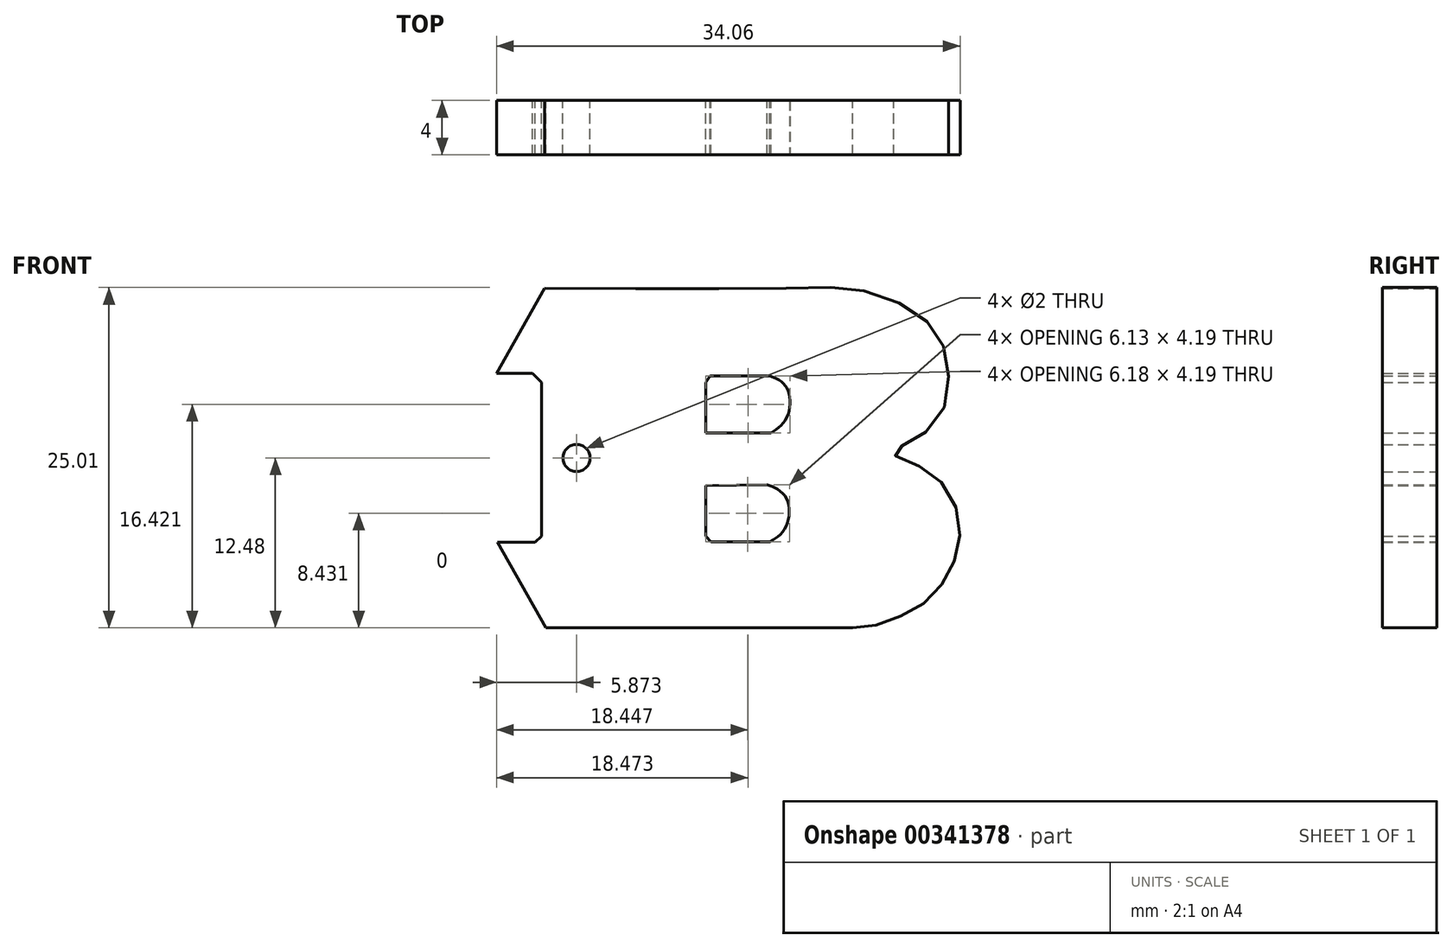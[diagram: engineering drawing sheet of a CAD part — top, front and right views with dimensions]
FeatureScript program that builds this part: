
annotation { "Feature Type Name" : "Feature", "Feature Type Description" : "" }
export const myFeature = defineFeature(function(context is Context, id is Id, definition is map)
    precondition{}
    {
        {
            var Q0;
            Q0=qCreatedBy(makeId("Front.planeOp"),FACE);
            var sketch = newSketch(context, id + "F0", { "sketchPlane" : qUnion([Q0])});
            skLineSegment(sketch, "E0", {"start": v(-1.02, 5.57) * mm, "end": v(-1.02, 1.85) * mm});
            skLineSegment(sketch, "E1", {"start": v(-1.02, 1.85) * mm, "end": v(3.76, 1.85) * mm});
            skLineSegment(sketch, "E2", {"start": v(3.68, 6.03) * mm, "end": v(-0.71, 6.03) * mm});
            skLineSegment(sketch, "E3", {"start": v(-0.71, 6.03) * mm, "end": v(-1.02, 5.57) * mm});
            skLineSegment(sketch, "E4", {"start": v(-1.02, -2.02) * mm, "end": v(-1.02, -5.76) * mm});
            skLineSegment(sketch, "E5", {"start": v(-1.02, -5.76) * mm, "end": v(-0.64, -6.14) * mm});
            skLineSegment(sketch, "E6", {"start": v(-0.64, -6.14) * mm, "end": v(3.68, -6.14) * mm});
            skLineSegment(sketch, "E7", {"start": v(-1.02, -2.02) * mm, "end": v(3.47, -1.95) * mm});
            skFitSpline(sketch, "E8", {"points": [v(3.68, -6.14) * mm, v(4.53, -5.54) * mm, v(5.05, -4.42) * mm, v(4.98, -3.13) * mm, v(4.25, -2.3) * mm, v(3.47, -1.95) * mm], "startDerivative": vector(4.7, 2.6) * mm, "endDerivative": vector(-4.47, 1.6) * mm});
            skFitSpline(sketch, "E9", {"points": [v(3.76, 1.85) * mm, v(4.58, 2.48) * mm, v(5.11, 3.54) * mm, v(5.07, 4.76) * mm, v(4.62, 5.53) * mm, v(3.68, 6.03) * mm], "startDerivative": vector(4.46, 2.83) * mm, "endDerivative": vector(-5.25, 2.14) * mm});
            skLineSegment(sketch, "E10", {"start": v(-12.8, -12.48) * mm, "end": v(9.75, -12.48) * mm});
            skFitSpline(sketch, "E11", {"points": [v(9.75, -12.48) * mm, v(11.48, -12.3) * mm, v(13.49, -11.51) * mm, v(15.31, -10.43) * mm, v(16.66, -8.76) * mm, v(17.48, -6.76) * mm, v(17.57, -4.42) * mm, v(16.44, -1.98) * mm, v(14.64, -0.58) * mm, v(12.84, 0.23) * mm, v(12.84, 0.57) * mm, v(14.1, 1.23) * mm, v(16.2, 3.12) * mm, v(16.82, 6.01) * mm, v(16.16, 8.8) * mm, v(14.12, 10.9) * mm, v(10.27, 12.35) * mm, v(6.04, 12.5) * mm, v(-12.87, 12.49) * mm], "startDerivative": vector(39.24, 1.65) * mm, "endDerivative": vector(-156.24, 0.65) * mm});
            skFitSpline(sketch, "E12", {"points": [v(-12.87, 12.49) * mm, v(-16.4, 6.2) * mm], "startDerivative": vector(-3.52, -6.28) * mm, "endDerivative": vector(-3.52, -6.28) * mm});
            skFitSpline(sketch, "E13", {"points": [v(-16.4, 6.2) * mm, v(-13.78, 6.2) * mm], "startDerivative": vector(2.62, 0) * mm, "endDerivative": vector(2.62, 0) * mm});
            skFitSpline(sketch, "E14", {"points": [v(-13.78, 6.2) * mm, v(-13.08, 5.55) * mm], "startDerivative": vector(0.7, -0.66) * mm, "endDerivative": vector(0.7, -0.66) * mm});
            skFitSpline(sketch, "E15", {"points": [v(-13.08, 5.55) * mm, v(-13.08, -5.75) * mm], "startDerivative": vector(0, -11.3) * mm, "endDerivative": vector(0, -11.3) * mm});
            skFitSpline(sketch, "E16", {"points": [v(-13.08, -5.75) * mm, v(-13.58, -6.2) * mm], "startDerivative": vector(-0.5, -0.45) * mm, "endDerivative": vector(-0.5, -0.45) * mm});
            skFitSpline(sketch, "E17", {"points": [v(-13.58, -6.2) * mm, v(-16.33, -6.2) * mm], "startDerivative": vector(-2.75, 0) * mm, "endDerivative": vector(-2.75, 0) * mm});
            skFitSpline(sketch, "E18", {"points": [v(-16.33, -6.2) * mm, v(-12.8, -12.48) * mm], "startDerivative": vector(3.54, -6.29) * mm, "endDerivative": vector(3.54, -6.29) * mm});
            skFitSpline(sketch, "E19", {"points": [v(-14.26, 13.78) * mm, v(10.52, 13.65) * mm], "startDerivative": vector(24.77, -0.13) * mm, "endDerivative": vector(24.77, -0.13) * mm});
            skFitSpline(sketch, "E20", {"points": [v(10.52, 13.65) * mm, v(14.21, 12.74) * mm, v(17.38, 10.62) * mm, v(18.6, 7.28) * mm, v(18.3, 3.41) * mm, v(15.72, 0.7) * mm], "startDerivative": vector(18.49, -3.32) * mm, "endDerivative": vector(-15.59, -12.12) * mm});
            skFitSpline(sketch, "E21", {"points": [v(15.72, 0.7) * mm, v(17.13, -0.58) * mm, v(19.32, -3.65) * mm, v(19.71, -8.34) * mm, v(15.72, -12.42) * mm, v(9.48, -13.89) * mm, v(1.15, -13.77) * mm, v(-14.57, -13.86) * mm], "startDerivative": vector(16.73, -14.1) * mm, "endDerivative": vector(-73.7, -1.28) * mm});
            skFitSpline(sketch, "E22", {"points": [v(-14.57, -13.86) * mm, v(-19.55, -5.16) * mm], "startDerivative": vector(-4.99, 8.7) * mm, "endDerivative": vector(-4.99, 8.7) * mm});
            skFitSpline(sketch, "E23", {"points": [v(-19.55, -5.16) * mm, v(-15.05, -5.16) * mm], "startDerivative": vector(4.5, 0) * mm, "endDerivative": vector(4.5, 0) * mm});
            skFitSpline(sketch, "E24", {"points": [v(-15.05, -5.16) * mm, v(-15.05, 5.06) * mm], "startDerivative": vector(0, 10.22) * mm, "endDerivative": vector(0, 10.22) * mm});
            skFitSpline(sketch, "E25", {"points": [v(-15.05, 5.06) * mm, v(-19.18, 5.06) * mm], "startDerivative": vector(-4.13, 0) * mm, "endDerivative": vector(-4.13, 0) * mm});
            skFitSpline(sketch, "E26", {"points": [v(-19.18, 5.06) * mm, v(-14.26, 13.78) * mm], "startDerivative": vector(4.92, 8.71) * mm, "endDerivative": vector(4.92, 8.71) * mm});
            skCircle(sketch, "E27", {"center": v(-10.53, 0) * mm, "radius": 1 * mm});
            skSolve(sketch);
        }
        {
            var Q0;
            Q0=makeQuery(id+"F0.imprint","IMPRINT",FACE,{"disambiguationData":[TD([[makeQuery(id+"F0.imprint","IMPRINT",EDGE,{"derivedFrom":sQuery(id+"F0.wireOp",EDGE,"E0")}),-1.0]])]});
            extrude(context, id + "F1", {"entities" : qUnion([Q0]), "depth" : 4 * mm});
        }
    });
